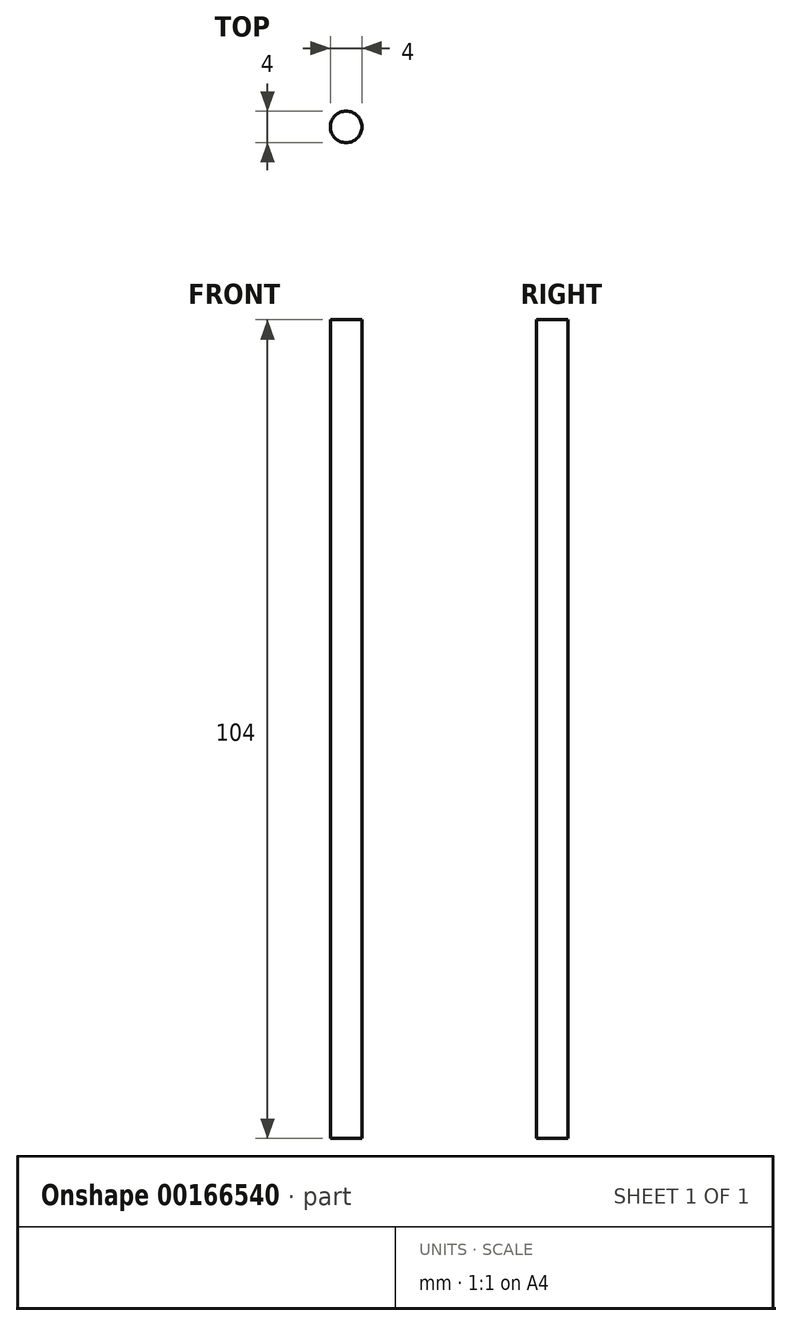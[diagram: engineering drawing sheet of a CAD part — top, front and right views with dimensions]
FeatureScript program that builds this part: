
annotation { "Feature Type Name" : "Feature", "Feature Type Description" : "" }
export const myFeature = defineFeature(function(context is Context, id is Id, definition is map)
    precondition{}
    {
        {
            var Q0;
            Q0=qCreatedBy(makeId("Top.planeOp"),FACE);
            var sketch = newSketch(context, id + "F0", { "sketchPlane" : qUnion([Q0])});
            skCircle(sketch, "E0", {"center": v(0, 0) * mm, "radius": 2 * mm});
            skSolve(sketch);
        }
        {
            var Q0;
            Q0=qSketchRegion(id+"F0",true);
            extrude(context, id + "F1", {"entities" : qUnion([Q0]), "depth" : 104 * mm});
        }
    });
